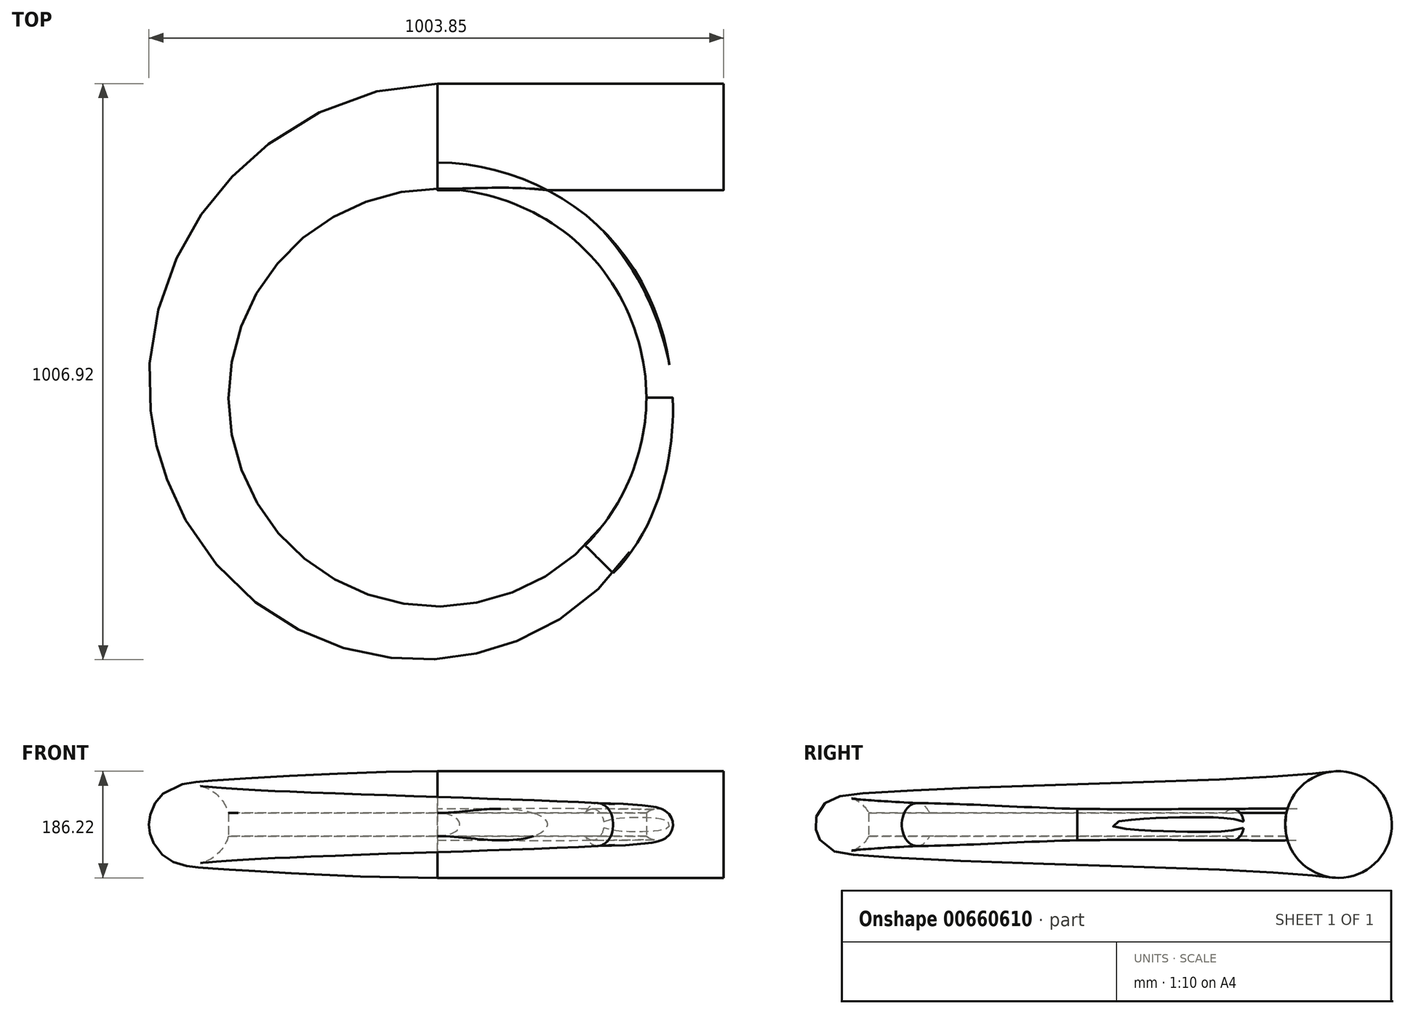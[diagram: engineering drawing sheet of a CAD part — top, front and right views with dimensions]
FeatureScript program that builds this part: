
annotation { "Feature Type Name" : "Feature", "Feature Type Description" : "" }
export const myFeature = defineFeature(function(context is Context, id is Id, definition is map)
    precondition{}
    {
        {
            var Q0;
            Q0=qCreatedBy(makeId("Top.planeOp"),FACE);
            var sketch = newSketch(context, id + "F0", { "sketchPlane" : qUnion([Q0])});
            skPoint(sketch, "E0", {"position": v(0, 365) * mm});
            skPoint(sketch, "E1", {"position": v(0, 465) * mm});
            skPoint(sketch, "E2", {"position": v(390, 0) * mm});
            skPoint(sketch, "E3", {"position": v(0, -415) * mm});
            skPoint(sketch, "E4", {"position": v(-440, 0) * mm});
            skPoint(sketch, "E5", {"position": v(-319.97, 319.97) * mm});
            skPoint(sketch, "E6", {"position": v(-302.29, -302.29) * mm});
            skPoint(sketch, "E7", {"position": v(284.61, -284.61) * mm});
            skPoint(sketch, "E8", {"position": v(266.93, 266.93) * mm});
            skPoint(sketch, "E9", {"position": v(0, 0) * mm});
            skEllipticalArc(sketch, "E10", {});
            skEllipticalArc(sketch, "E11", {});
            skEllipticalArc(sketch, "E12", {});
            skEllipticalArc(sketch, "E13", {});
            skEllipticalArc(sketch, "E14", {});
            skEllipticalArc(sketch, "E15", {});
            skEllipticalArc(sketch, "E16", {});
            skEllipticalArc(sketch, "E17", {});
            const initialGuessF0  = {"E10": [0, 0, -1, 0, 0.44, 0.46612968872584987, 5.526615742997421, 6.283185307179586], "E11": [0, 0, -0.7071067811865476, 0.7071067811865476, 0.4525, 0.4785966473523233, 5.52580766897991, 6.283185307179586], "E12": [0, 0, -1, 0, 0.44, 0.4160081858272839, 0, 0.8134183801700188], "E13": [0, 0, 0, -1, 0.415, 0.44120212867656267, 5.528380332844562, 6.283185307179586], "E14": [0, 0, 0.7071067811865496, -0.7071067811865456, 0.4025, 0.428741948548535, 5.529346229436823, 6.283185307179586], "E15": [0, 0, 1, 0, 0.39, 0.41628449735106027, 5.530375135076127, 6.283185307179586], "E16": [0, 0, 0.7071067811865476, 0.7071067811865476, 0.3775, 0.4038300656260106, 5.531473426373671, 6.283185307179586], "E17": [0, 0, 0, 1, 0.365, 0.3913789866865713, 5.532648370907622, 6.283185307179586]};
            skSetInitialGuess(sketch, initialGuessF0);
            skSolve(sketch);
        }
        {
            var Q0;
            Q0=qCreatedBy(makeId("Top.planeOp"),FACE);
            cPlane(context, id + "F1", {"entities" : qUnion([Q0]), "cplaneType" : CPlaneType.OFFSET, "offset" : 20.2 * mm, "width" : 150 * mm, "height" : 150 * mm});
        }
        {
            var Q0;
            Q0=qCreatedBy(id+"F1.planeOp",FACE);
            var sketch = newSketch(context, id + "F2", { "sketchPlane" : qUnion([Q0])});
            skPoint(sketch, "E18", {"position": v(0, 365) * mm});
            skPoint(sketch, "E19", {"position": v(0, 465) * mm});
            skPoint(sketch, "E20", {"position": v(390, 0) * mm});
            skPoint(sketch, "E21", {"position": v(0, -415) * mm});
            skPoint(sketch, "E22", {"position": v(-440, 0) * mm});
            skPoint(sketch, "E23", {"position": v(-319.97, 319.97) * mm});
            skPoint(sketch, "E24", {"position": v(-302.29, -302.29) * mm});
            skPoint(sketch, "E25", {"position": v(284.61, -284.61) * mm});
            skPoint(sketch, "E26", {"position": v(266.93, 266.93) * mm});
            skPoint(sketch, "E27", {"position": v(0, 0) * mm});
            skEllipticalArc(sketch, "E28", {});
            skEllipticalArc(sketch, "E29", {});
            skEllipticalArc(sketch, "E30", {});
            skEllipticalArc(sketch, "E31", {});
            skEllipticalArc(sketch, "E32", {});
            skEllipticalArc(sketch, "E33", {});
            skEllipticalArc(sketch, "E34", {});
            skEllipticalArc(sketch, "E35", {});
            const initialGuessF2  = {"E28": [0, 0, -1, 0, 0.44, 0.46612968872584987, 5.526615742997423, 6.283185307179586], "E29": [0, 0, -0.7071067811865476, 0.7071067811865476, 0.4525, 0.4785966473523233, 5.52580766897991, 6.283185307179586], "E30": [0, 0, -1, 0, 0.44, 0.4160081858272839, 0, 0.813418380170019], "E31": [0, 0, 0, -1, 0.415, 0.44120212867656267, 5.528380332844563, 6.283185307179586], "E32": [0, 0, 0.7071067811865496, -0.7071067811865456, 0.4025, 0.428741948548535, 5.529346229436822, 6.283185307179586], "E33": [0, 0, 1, 0, 0.39, 0.41628449735106027, 5.530375135076128, 6.283185307179586], "E34": [0, 0, 0.7071067811865476, 0.7071067811865476, 0.3775, 0.4038300656260106, 5.531473426373671, 6.283185307179586], "E35": [0, 0, 0, 1, 0.365, 0.3913789866865713, 5.532648370907622, 6.283185307179586]};
            skSetInitialGuess(sketch, initialGuessF2);
            skSolve(sketch);
        }
        {
            var Q0;
            Q0=sQuery(id+"F2.wireOp",VERTEX,"E24");
            var Q1;
            Q1=sQuery(id+"F0.wireOp",VERTEX,"E10.center");
            var Q2;
            Q2=sQuery(id+"F2.wireOp",VERTEX,"E26");
            cPlane(context, id + "F3", {"entities" : qUnion([Q0, Q1, Q2]), "cplaneType" : CPlaneType.THREE_POINT, "offset" : 25 * mm, "width" : 150 * mm, "height" : 150 * mm});
        }
        {
            var Q0;
            Q0=sQuery(id+"F2.wireOp",VERTEX,"E23");
            var Q1;
            Q1=sQuery(id+"F0.wireOp",VERTEX,"E9");
            var Q2;
            Q2=sQuery(id+"F2.wireOp",VERTEX,"E25");
            cPlane(context, id + "F4", {"entities" : qUnion([Q0, Q1, Q2]), "cplaneType" : CPlaneType.THREE_POINT, "offset" : 25 * mm, "width" : 150 * mm, "height" : 150 * mm});
        }
        {
            var Q0;
            Q0=qCreatedBy(makeId("Top.planeOp"),FACE);
            cPlane(context, id + "F5", {"entities" : qUnion([Q0]), "cplaneType" : CPlaneType.OFFSET, "offset" : 40.4 * mm, "width" : 150 * mm, "height" : 150 * mm});
        }
        {
            var Q0;
            Q0=qCreatedBy(makeId("Top.planeOp"),FACE);
            var sketch = newSketch(context, id + "F6", { "sketchPlane" : qUnion([Q0])});
            skCircle(sketch, "E36", {"center": v(0, 0) * mm, "radius": 365 * mm});
            skSolve(sketch);
        }
        {
            var Q0;
            Q0=qCreatedBy(makeId("Right.planeOp"),FACE);
            var sketch = newSketch(context, id + "F7", { "sketchPlane" : qUnion([Q0])});
            skPoint(sketch, "E37", {"position": v(365, 0) * mm});
            skPoint(sketch, "E38", {"position": v(365, 40.4) * mm});
            skPoint(sketch, "E39", {"position": v(411, 20.2) * mm});
            skArc(sketch, "E40", {"start": v(365, 0) * mm, "mid": v(411, 20.2) * mm, "end": v(365, 40.4) * mm});
            skLineSegment(sketch, "E41", {"start": v(365, 40.4) * mm, "end": v(365, 0) * mm});
            skSolve(sketch);
        }
        {
            var Q0;
            Q0=qCreatedBy(makeId("Right.planeOp"),FACE);
            var sketch = newSketch(context, id + "F8", { "sketchPlane" : qUnion([Q0])});
            skPoint(sketch, "E42", {"position": v(-365, 0) * mm});
            skPoint(sketch, "E43", {"position": v(-365, 40.4) * mm});
            skPoint(sketch, "E44", {"position": v(-457, 20.2) * mm});
            skArc(sketch, "E45", {"start": v(-365, 40.4) * mm, "mid": v(-457, 20.2) * mm, "end": v(-365, 0) * mm});
            skLineSegment(sketch, "E46", {"start": v(-365, 40.4) * mm, "end": v(-365, 0) * mm});
            skSolve(sketch);
        }
        {
            var Q0;
            Q0=qCreatedBy(makeId("Right.planeOp"),FACE);
            var sketch = newSketch(context, id + "F9", { "sketchPlane" : qUnion([Q0])});
            skPoint(sketch, "E47", {"position": v(365, 40.4) * mm});
            skPoint(sketch, "E48", {"position": v(365, 0) * mm});
            skPoint(sketch, "E49", {"position": v(549, 20.2) * mm});
            skArc(sketch, "E50", {"start": v(365, 0) * mm, "mid": v(549, 20.2) * mm, "end": v(365, 40.4) * mm});
            skLineSegment(sketch, "E51", {"start": v(365, 40.4) * mm, "end": v(365, 0) * mm});
            skSolve(sketch);
        }
        {
            var Q0;
            Q0=qCreatedBy(makeId("Front.planeOp"),FACE);
            var sketch = newSketch(context, id + "F10", { "sketchPlane" : qUnion([Q0])});
            skPoint(sketch, "E52", {"position": v(365, 0) * mm});
            skPoint(sketch, "E53", {"position": v(365, 40.4) * mm});
            skPoint(sketch, "E54", {"position": v(411, 20.2) * mm});
            skArc(sketch, "E55", {"start": v(365, 0) * mm, "mid": v(411, 20.2) * mm, "end": v(365, 40.4) * mm});
            skLineSegment(sketch, "E56", {"start": v(365, 40.4) * mm, "end": v(365, 0) * mm});
            skSolve(sketch);
        }
        {
            var Q0;
            Q0=qCreatedBy(makeId("Front.planeOp"),FACE);
            var sketch = newSketch(context, id + "F11", { "sketchPlane" : qUnion([Q0])});
            skPoint(sketch, "E57", {"position": v(-365, 40.4) * mm});
            skPoint(sketch, "E58", {"position": v(-365, 0) * mm});
            skPoint(sketch, "E59", {"position": v(-503, 20.2) * mm});
            skArc(sketch, "E60", {"start": v(-365, 40.4) * mm, "mid": v(-503, 20.2) * mm, "end": v(-365, 0) * mm});
            skLineSegment(sketch, "E61", {"start": v(-365, 40.4) * mm, "end": v(-365, 0) * mm});
            skSolve(sketch);
        }
        {
            var Q0;
            Q0=qCreatedBy(id+"F3.planeOp",FACE);
            var sketch = newSketch(context, id + "F12", { "sketchPlane" : qUnion([Q0])});
            skPoint(sketch, "E62", {"position": v(-365, 0) * mm});
            skPoint(sketch, "E63", {"position": v(-365, 40.4) * mm});
            skPoint(sketch, "E64", {"position": v(-411, 20.2) * mm});
            skArc(sketch, "E65", {"start": v(-365, 40.4) * mm, "mid": v(-411, 20.2) * mm, "end": v(-365, 0) * mm});
            skLineSegment(sketch, "E66", {"start": v(-365, 40.4) * mm, "end": v(-365, 0) * mm});
            skSolve(sketch);
        }
        {
            var Q0;
            Q0=qCreatedBy(id+"F3.planeOp",FACE);
            var sketch = newSketch(context, id + "F13", { "sketchPlane" : qUnion([Q0])});
            skPoint(sketch, "E67", {"position": v(365, 0) * mm});
            skPoint(sketch, "E68", {"position": v(365, 40.4) * mm});
            skPoint(sketch, "E69", {"position": v(480, 20.2) * mm});
            skArc(sketch, "E70", {"start": v(365, 0) * mm, "mid": v(480, 20.2) * mm, "end": v(365, 40.4) * mm});
            skLineSegment(sketch, "E71", {"start": v(365, 40.4) * mm, "end": v(365, 0) * mm});
            skSolve(sketch);
        }
        {
            var Q0;
            Q0=qCreatedBy(id+"F4.planeOp",FACE);
            var sketch = newSketch(context, id + "F14", { "sketchPlane" : qUnion([Q0])});
            skPoint(sketch, "E72", {"position": v(-365, 0) * mm});
            skPoint(sketch, "E73", {"position": v(-365, 40.4) * mm});
            skPoint(sketch, "E74", {"position": v(-434, 20.2) * mm});
            skArc(sketch, "E75", {"start": v(-365, 40.4) * mm, "mid": v(-434, 20.2) * mm, "end": v(-365, 0) * mm});
            skLineSegment(sketch, "E76", {"start": v(-365, 40.4) * mm, "end": v(-365, 0) * mm});
            skSolve(sketch);
        }
        {
            var Q0;
            Q0=qCreatedBy(id+"F4.planeOp",FACE);
            var sketch = newSketch(context, id + "F15", { "sketchPlane" : qUnion([Q0])});
            skPoint(sketch, "E77", {"position": v(365, 0) * mm});
            skPoint(sketch, "E78", {"position": v(365, 40.4) * mm});
            skPoint(sketch, "E79", {"position": v(526, 20.2) * mm});
            skArc(sketch, "E80", {"start": v(365, 0) * mm, "mid": v(526, 20.2) * mm, "end": v(365, 40.4) * mm});
            skLineSegment(sketch, "E81", {"start": v(365, 40.4) * mm, "end": v(365, 0) * mm});
            skSolve(sketch);
        }
        {
            var Q0;
            Q0=makeQuery(id+"F9.imprint","IMPRINT",FACE,{"disambiguationData":[TD([[makeQuery(id+"F9.imprint","IMPRINT",EDGE,{"derivedFrom":sQuery(id+"F9.wireOp",EDGE,"E50")}),1.0]])]});
            var Q1;
            Q1=makeQuery(id+"F15.imprint","IMPRINT",FACE,{"disambiguationData":[TD([[makeQuery(id+"F15.imprint","IMPRINT",EDGE,{"derivedFrom":sQuery(id+"F15.wireOp",EDGE,"E80")}),1.0]])]});
            var Q2;
            Q2=makeQuery(id+"F11.imprint","IMPRINT",FACE,{"disambiguationData":[TD([[makeQuery(id+"F11.imprint","IMPRINT",EDGE,{"derivedFrom":sQuery(id+"F11.wireOp",EDGE,"E60")}),1.0]])]});
            var Q3;
            Q3=makeQuery(id+"F13.imprint","IMPRINT",FACE,{"disambiguationData":[TD([[makeQuery(id+"F13.imprint","IMPRINT",EDGE,{"derivedFrom":sQuery(id+"F13.wireOp",EDGE,"E70")}),1.0]])]});
            var Q4;
            Q4=makeQuery(id+"F8.imprint","IMPRINT",FACE,{"disambiguationData":[TD([[makeQuery(id+"F8.imprint","IMPRINT",EDGE,{"derivedFrom":sQuery(id+"F8.wireOp",EDGE,"E45")}),1.0]])]});
            var Q5;
            Q5=makeQuery(id+"F14.imprint","IMPRINT",FACE,{"disambiguationData":[TD([[makeQuery(id+"F14.imprint","IMPRINT",EDGE,{"derivedFrom":sQuery(id+"F14.wireOp",EDGE,"E75")}),1.0]])]});
            var Q6;
            Q6=makeQuery(id+"F10.imprint","IMPRINT",FACE,{"disambiguationData":[TD([[makeQuery(id+"F10.imprint","IMPRINT",EDGE,{"derivedFrom":sQuery(id+"F10.wireOp",EDGE,"E55")}),1.0]])]});
            var Q7;
            Q7=makeQuery(id+"F12.imprint","IMPRINT",FACE,{"disambiguationData":[TD([[makeQuery(id+"F12.imprint","IMPRINT",EDGE,{"derivedFrom":sQuery(id+"F12.wireOp",EDGE,"E65")}),1.0]])]});
            var Q8;
            Q8=qConstructionFilter(qBodyType(qCreatedBy(id+"F9",EDGE),BodyType.WIRE),ConstructionObject.NO);
            var Q9;
            Q9=qConstructionFilter(qBodyType(qCreatedBy(id+"F15",EDGE),BodyType.WIRE),ConstructionObject.NO);
            var Q10;
            Q10=qConstructionFilter(qBodyType(qCreatedBy(id+"F11",EDGE),BodyType.WIRE),ConstructionObject.NO);
            var Q11;
            Q11=sQuery(id+"F13.wireOp",EDGE,"E70");
            var Q12;
            Q12=sQuery(id+"F8.wireOp",EDGE,"E45");
            loft(context, id + "F16", {"startCondition" : LoftEndDerivativeType.NORMAL_TO_PROFILE, "startMagnitude" : 1, "endCondition" : LoftEndDerivativeType.NORMAL_TO_PROFILE, "endMagnitude" : 1, "sheetProfilesArray" : [{ "sheetProfileEntities" : qUnion([Q0]) }, { "sheetProfileEntities" : qUnion([Q1]) }, { "sheetProfileEntities" : qUnion([Q2]) }, { "sheetProfileEntities" : qUnion([Q3]) }, { "sheetProfileEntities" : qUnion([Q4]) }, { "sheetProfileEntities" : qUnion([Q5]) }, { "sheetProfileEntities" : qUnion([Q6]) }, { "sheetProfileEntities" : qUnion([Q7]) }], "wireProfilesArray" : [{ "wireProfileEntities" : qUnion([Q8]) }, { "wireProfileEntities" : qUnion([Q9]) }, { "wireProfileEntities" : qUnion([Q10]) }, { "wireProfileEntities" : qUnion([Q11]) }, { "wireProfileEntities" : qUnion([Q12]) }]});
        }
        {
            var Q0;
            Q0=qCreatedBy(makeId("Right.planeOp"),FACE);
            var sketch = newSketch(context, id + "F17", { "sketchPlane" : qUnion([Q0])});
            skPoint(sketch, "E82", {"position": v(365, 40.4) * mm});
            skPoint(sketch, "E83", {"position": v(365, 0) * mm});
            skPoint(sketch, "E84", {"position": v(549, 19.97) * mm});
            skCircle(sketch, "E85", {"center": v(455.9, 20.2) * mm, "radius": 93.1 * mm});
            skSolve(sketch);
        }
        {
            var Q0;
            Q0=qSketchRegion(id+"F17",true);
            var Q1;
            Q1=qConstructionFilter(qBodyType(qCreatedBy(id+"F17",EDGE),BodyType.WIRE),ConstructionObject.NO);
            extrude(context, id + "F18", {"entities" : qUnion([Q0]), "operationType" : NewBodyOperationType.ADD, "surfaceEntities" : qUnion([Q1]), "depth" : 500 * mm, "offsetDistance" : 25 * mm});
        }
        {
            var Q0;
            Q0=qSketchRegion(id+"F14",true);
            var Q1;
            Q1=qSketchRegion(id+"F10",true);
            var Q2;
            Q2=qSketchRegion(id+"F12",true);
            var Q3;
            Q3=qSketchRegion(id+"F7",true);
            var Q4;
            Q4=qConstructionFilter(qBodyType(qCreatedBy(id+"F10",EDGE),BodyType.WIRE),ConstructionObject.NO);
            var Q5;
            Q5=qConstructionFilter(qBodyType(qCreatedBy(id+"F12",EDGE),BodyType.WIRE),ConstructionObject.NO);
            var Q6;
            Q6=qConstructionFilter(qBodyType(qCreatedBy(id+"F7",EDGE),BodyType.WIRE),ConstructionObject.NO);
            loft(context, id + "F19", {"operationType" : NewBodyOperationType.ADD, "startCondition" : LoftEndDerivativeType.NORMAL_TO_PROFILE, "startMagnitude" : 1, "endCondition" : LoftEndDerivativeType.NORMAL_TO_PROFILE, "endMagnitude" : 1, "sheetProfilesArray" : [{ "sheetProfileEntities" : qUnion([Q0]) }, { "sheetProfileEntities" : qUnion([Q1]) }, { "sheetProfileEntities" : qUnion([Q2]) }, { "sheetProfileEntities" : qUnion([Q3]) }], "wireProfilesArray" : [{ "wireProfileEntities" : qUnion([Q4]) }, { "wireProfileEntities" : qUnion([Q5]) }, { "wireProfileEntities" : qUnion([Q6]) }]});
        }
        {
            var Q0;
            Q0=qCreatedBy(makeId("Front.planeOp"),FACE);
            var sketch = newSketch(context, id + "F20", { "sketchPlane" : qUnion([Q0])});
            skLineSegment(sketch, "E86", {"start": v(0, 65.38) * mm, "end": v(0, -33.02) * mm});
            skSolve(sketch);
        }
        {
            var Q0;
            Q0=qSketchRegion(id+"F17",true);
            var Q1;
            Q1=qConstructionFilter(qBodyType(qCreatedBy(id+"F17",EDGE),BodyType.WIRE),ConstructionObject.NO);
            extrude(context, id + "F21", {"entities" : qUnion([Q0]), "bodyType" : ToolBodyType.SURFACE, "surfaceEntities" : qUnion([Q1]), "depth" : 500 * mm, "offsetDistance" : 25 * mm});
        }
    });
